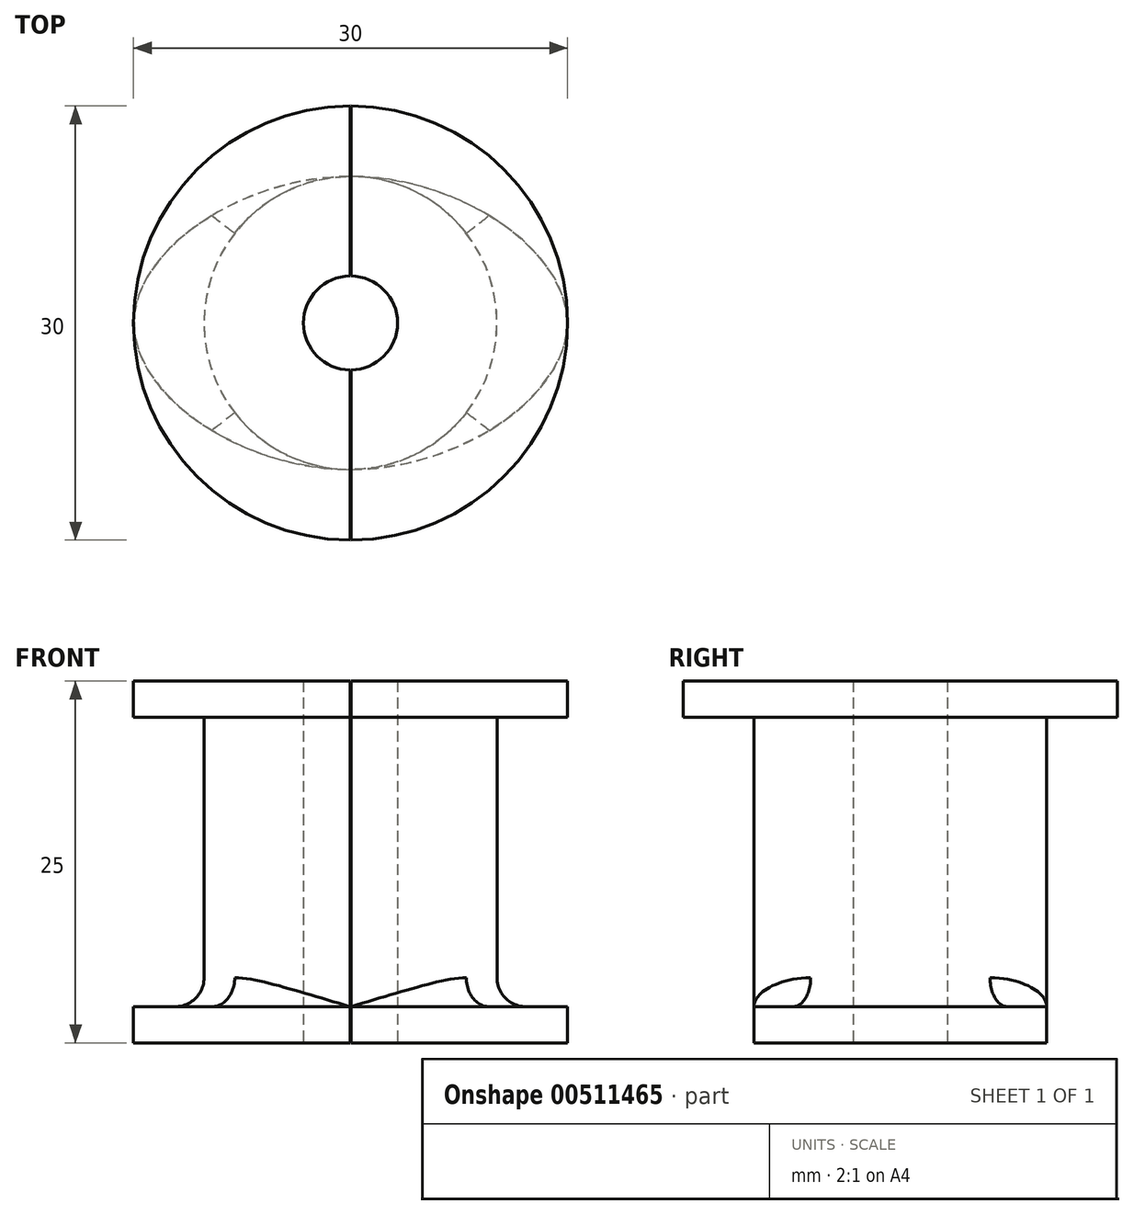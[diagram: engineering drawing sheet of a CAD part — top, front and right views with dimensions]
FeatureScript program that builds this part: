
annotation { "Feature Type Name" : "Feature", "Feature Type Description" : "" }
export const myFeature = defineFeature(function(context is Context, id is Id, definition is map)
    precondition{}
    {
        {
            var Q0;
            Q0=qCreatedBy(makeId("Top.planeOp"),FACE);
            var sketch = newSketch(context, id + "F0", { "sketchPlane" : qUnion([Q0])});
            skCircle(sketch, "E0", {"center": v(0, 0) * mm, "radius": 15 * mm});
            skCircle(sketch, "E1", {"center": v(0, 0) * mm, "radius": 3.25 * mm});
            skSolve(sketch);
        }
        {
            var Q0;
            Q0 = qSketchRegion(id + "F0", true);
            extrude(context, id + "F1", {"entities" : qUnion([Q0]), "depth" : 2.5 * mm, "offsetDistance" : 25 * mm});
        }
        {
            var Q0;
            Q0=makeQuery(id+"F1.opExtrude","CAP_FACE",FACE,{"disambiguationData":[OSD([sQuery(id+"F0.wireOp",EDGE,"E0"),sQuery(id+"F0.wireOp",EDGE,"E1")])],"isStart":true});
            var sketch = newSketch(context, id + "F2", { "sketchPlane" : qUnion([Q0])});
            skCircle(sketch, "E2", {"center": v(0, 0) * mm, "radius": 10.12 * mm});
            skCircle(sketch, "E3", {"center": v(0, 0) * mm, "radius": 3.25 * mm});
            skSolve(sketch);
        }
        {
            var Q0;
            Q0=makeQuery(id+"F2.imprint","IMPRINT",FACE,{"disambiguationData":[TD([[makeQuery(id+"F2.imprint","IMPRINT",EDGE,{"derivedFrom":sQuery(id+"F2.wireOp",EDGE,"E2")}),1.0]])]});
            extrude(context, id + "F3", {"entities" : qUnion([Q0]), "operationType" : NewBodyOperationType.ADD, "depth" : 20 * mm, "offsetDistance" : 25 * mm});
        }
        {
            var Q0;
            Q0=makeQuery(id+"F3.opExtrude","CAP_FACE",FACE,{"disambiguationData":[OSD([sQuery(id+"F2.wireOp",EDGE,"E2"),sQuery(id+"F2.wireOp",EDGE,"E3")])],"isStart":false});
            var sketch = newSketch(context, id + "F4", { "sketchPlane" : qUnion([Q0])});
            skLineSegment(sketch, "E4.bottom", {"start": v(-15, -10.12) * mm, "end": v(15, -10.12) * mm, "construction": true});
            skLineSegment(sketch, "E4.top", {"start": v(-15, 10.12) * mm, "end": v(15, 10.12) * mm, "construction": true});
            skLineSegment(sketch, "E4.left", {"start": v(-15, -10.12) * mm, "end": v(-15, 10.12) * mm, "construction": true});
            skLineSegment(sketch, "E4.right", {"start": v(15, -10.12) * mm, "end": v(15, 10.12) * mm, "construction": true});
            skPoint(sketch, "E4.middle", {"position": v(0, 0) * mm});
            skLineSegment(sketch, "E5", {"start": v(0, 10.12) * mm, "end": v(0, -10.12) * mm, "construction": true});
            skLineSegment(sketch, "E6", {"start": v(-15, 0) * mm, "end": v(15, 0) * mm, "construction": true});
            skFitSpline(sketch, "E7", {"points": [v(0, 10.12) * mm, v(15, 0) * mm, v(0, -10.12) * mm, v(-15, 0) * mm, v(0, 10.12) * mm]});
            skSolve(sketch);
        }
        {
            var Q0;
            {var subQ0=sQuery(id+"F4.wireOp",EDGE,"E7");var subQ1=makeQuery(id+"F3.opExtrude","CAP_EDGE",EDGE,{"disambiguationData":[OSD([sQuery(id+"F2.wireOp",EDGE,"E2")])],"isStart":false});var subQ2=makeQuery(id+"F4.imprint","INTERSECT",VERTEX,{"disambiguationData":[OD(0.0)],"derivedFrom":[subQ1,subQ0]});Q0=makeQuery(id+"F4.imprint","IMPRINT",FACE,{"disambiguationData":[TD([[makeQuery(id+"F4.imprint","IMPRINT",EDGE,{"disambiguationData":[TD([[subQ2,1.0]])],"derivedFrom":subQ0}),-1.0]])]});}
            var Q1;
            Q1=makeQuery(id+"F4.imprint","IMPRINT",FACE,{"disambiguationData":[TD([[makeQuery(id+"F4.imprint","IMPRINT",EDGE,{"derivedFrom":makeQuery(id+"F3.opExtrude","CAP_EDGE",EDGE,{"disambiguationData":[OSD([sQuery(id+"F2.wireOp",EDGE,"E3")])],"isStart":false})}),1.0]])]});
            var Q2;
            {var subQ0=sQuery(id+"F4.wireOp",EDGE,"E7");var subQ1=makeQuery(id+"F3.opExtrude","CAP_EDGE",EDGE,{"disambiguationData":[OSD([sQuery(id+"F2.wireOp",EDGE,"E2")])],"isStart":false});var subQ2=makeQuery(id+"F4.imprint","INTERSECT",VERTEX,{"disambiguationData":[OD(0.0)],"derivedFrom":[subQ1,subQ0]});Q2=makeQuery(id+"F4.imprint","IMPRINT",FACE,{"disambiguationData":[TD([[makeQuery(id+"F4.imprint","IMPRINT",EDGE,{"disambiguationData":[TD([[subQ2,-1.0]])],"derivedFrom":subQ0}),-1.0]])]});}
            extrude(context, id + "F5", {"entities" : qUnion([Q0, Q1, Q2]), "operationType" : NewBodyOperationType.ADD, "depth" : 2.5 * mm, "offsetDistance" : 25 * mm});
        }
        {
            var Q0;
            Q0=makeQuery(id+"F5.boolean.opBoolean","SPLIT",EDGE,{"disambiguationData":[OD(1.0)],"derivedFrom":makeQuery(id+"F3.opExtrude","CAP_EDGE",EDGE,{"disambiguationData":[OSD([sQuery(id+"F2.wireOp",EDGE,"E2")])],"isStart":false})});
            var Q1;
            Q1=makeQuery(id+"F5.boolean.opBoolean","SPLIT",EDGE,{"disambiguationData":[OD(0.0)],"derivedFrom":makeQuery(id+"F3.opExtrude","CAP_EDGE",EDGE,{"disambiguationData":[OSD([sQuery(id+"F2.wireOp",EDGE,"E2")])],"isStart":false})});
            var Q2;
            Q2=makeQuery(id+"F3.opExtrude","CAP_EDGE",EDGE,{"disambiguationData":[OSD([sQuery(id+"F2.wireOp",EDGE,"E2")])],"isStart":true});
            fillet(context, id + "F6", {"entities" : qUnion([Q0, Q1, Q2]), "tangentPropagation" : true, "radius" : 2 * mm, "defaultsChanged" : false, "vertexSettings" : [], "allowEdgeOverflow" : false});
        }
        {
            var Q0;
            Q0=makeQuery(id+"F1.opExtrude","CAP_FACE",FACE,{"disambiguationData":[OSD([sQuery(id+"F0.wireOp",EDGE,"E0"),sQuery(id+"F0.wireOp",EDGE,"E1")])],"isStart":false});
            var sketch = newSketch(context, id + "F7", { "sketchPlane" : qUnion([Q0])});
            skLineSegment(sketch, "E8.bottom", {"start": v(-0.03, -22.5) * mm, "end": v(0.03, -22.5) * mm});
            skLineSegment(sketch, "E8.top", {"start": v(-0.03, 22.5) * mm, "end": v(0.03, 22.5) * mm});
            skLineSegment(sketch, "E8.left", {"start": v(-0.03, -22.5) * mm, "end": v(-0.03, 22.5) * mm});
            skLineSegment(sketch, "E8.right", {"start": v(0.03, -22.5) * mm, "end": v(0.03, 22.5) * mm});
            skPoint(sketch, "E8.middle", {"position": v(0, 0) * mm});
            skSolve(sketch);
        }
        {
            var Q0;
            {var subQ0=sQuery(id+"F7.wireOp",EDGE,"E8.top");Q0=makeQuery(id+"F7.imprint","IMPRINT",FACE,{"disambiguationData":[TD([[makeQuery(id+"F7.imprint","IMPRINT",EDGE,{"derivedFrom":subQ0}),-1.0]])]});}
            var Q1;
            {var subQ0=sQuery(id+"F7.wireOp",EDGE,"E8.left");var subQ1=makeQuery(id+"F1.opExtrude","CAP_EDGE",EDGE,{"disambiguationData":[OSD([sQuery(id+"F0.wireOp",EDGE,"E0")])],"isStart":false});var subQ2=makeQuery(id+"F7.imprint","INTERSECT",VERTEX,{"disambiguationData":[OD(1.0)],"derivedFrom":[subQ1,subQ0]});Q1=makeQuery(id+"F7.imprint","IMPRINT",FACE,{"disambiguationData":[TD([[makeQuery(id+"F7.imprint","IMPRINT",EDGE,{"disambiguationData":[TD([[subQ2,1.0]])],"derivedFrom":subQ0}),-1.0]])]});}
            var Q2;
            {var subQ0=sQuery(id+"F7.wireOp",EDGE,"E8.bottom");Q2=makeQuery(id+"F7.imprint","IMPRINT",FACE,{"disambiguationData":[TD([[makeQuery(id+"F7.imprint","IMPRINT",EDGE,{"derivedFrom":subQ0}),1.0]])]});}
            var Q3;
            {var subQ0=sQuery(id+"F7.wireOp",EDGE,"E8.left");var subQ1=makeQuery(id+"F1.opExtrude","CAP_EDGE",EDGE,{"disambiguationData":[OSD([sQuery(id+"F0.wireOp",EDGE,"E0")])],"isStart":false});var subQ2=makeQuery(id+"F7.imprint","INTERSECT",VERTEX,{"disambiguationData":[OD(0.0)],"derivedFrom":[subQ1,subQ0]});Q3=makeQuery(id+"F7.imprint","IMPRINT",FACE,{"disambiguationData":[TD([[makeQuery(id+"F7.imprint","IMPRINT",EDGE,{"disambiguationData":[TD([[subQ2,-1.0]])],"derivedFrom":subQ0}),-1.0]])]});}
            var Q4;
            {var subQ0=sQuery(id+"F7.wireOp",EDGE,"E8.left");var subQ1=makeQuery(id+"F1.opExtrude","CAP_EDGE",EDGE,{"disambiguationData":[OSD([sQuery(id+"F0.wireOp",EDGE,"E1")])],"isStart":false});var subQ2=makeQuery(id+"F7.imprint","INTERSECT",VERTEX,{"disambiguationData":[OD(0.0)],"derivedFrom":[subQ1,subQ0]});Q4=makeQuery(id+"F7.imprint","IMPRINT",FACE,{"disambiguationData":[TD([[makeQuery(id+"F7.imprint","IMPRINT",EDGE,{"disambiguationData":[TD([[subQ2,-1.0]])],"derivedFrom":subQ0}),-1.0]])]});}
            extrude(context, id + "F8", {"entities" : qUnion([Q0, Q1, Q2, Q3, Q4]), "operationType" : NewBodyOperationType.REMOVE, "endBound" : BoundingType.THROUGH_ALL, "oppositeDirection" : true, "depth" : 25 * mm, "offsetDistance" : 25 * mm});
        }
    });
